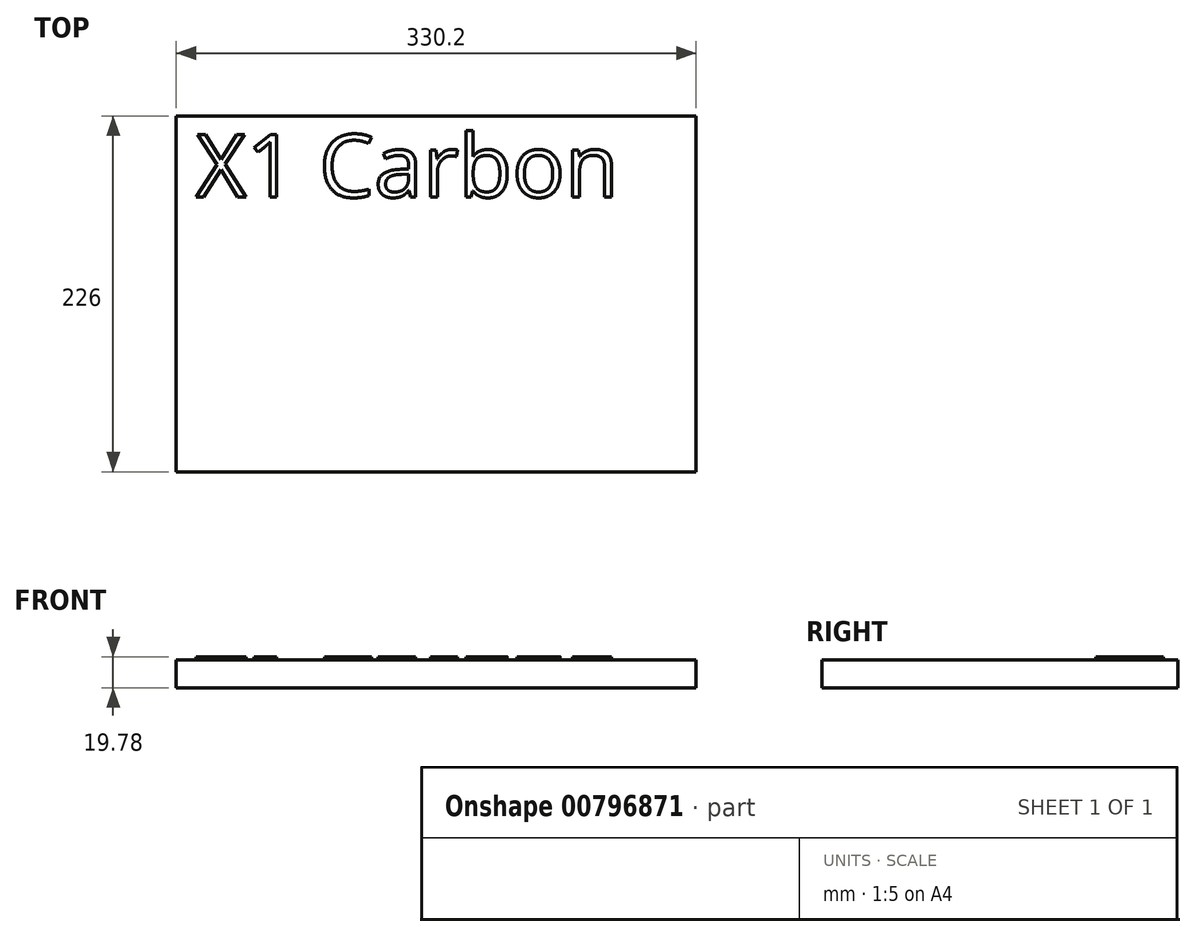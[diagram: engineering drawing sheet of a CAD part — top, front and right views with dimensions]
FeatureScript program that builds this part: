
annotation { "Feature Type Name" : "Feature", "Feature Type Description" : "" }
export const myFeature = defineFeature(function(context is Context, id is Id, definition is map)
    precondition{}
    {
        {
            var Q0;
            Q0=qCreatedBy(makeId("Top.planeOp"),FACE);
            var sketch = newSketch(context, id + "F0", { "sketchPlane" : qUnion([Q0])});
            skLineSegment(sketch, "E0.bottom", {"start": v(-174.06, 110.55) * mm, "end": v(156.14, 110.55) * mm});
            skLineSegment(sketch, "E0.top", {"start": v(-174.06, -115.45) * mm, "end": v(156.14, -115.45) * mm});
            skLineSegment(sketch, "E0.left", {"start": v(-174.06, 110.55) * mm, "end": v(-174.06, -115.45) * mm});
            skLineSegment(sketch, "E0.right", {"start": v(156.14, 110.55) * mm, "end": v(156.14, -115.45) * mm});
            skSolve(sketch);
        }
        {
            var Q0;
            Q0=makeQuery(id+"F0.imprint","IMPRINT",FACE,{"disambiguationData":[TD([[makeQuery(id+"F0.imprint","IMPRINT",EDGE,{"derivedFrom":sQuery(id+"F0.wireOp",EDGE,"E0.bottom")}),-1.0]])]});
            extrude(context, id + "F1", {"entities" : qUnion([Q0]), "depth" : 17.78 * mm, "offsetDistance" : 25 * mm});
        }
        {
            var Q0;
            Q0=makeQuery(id+"F1.opExtrude","CAP_FACE",FACE,{"disambiguationData":[OSD([sQuery(id+"F0.wireOp",EDGE,"E0.bottom"),sQuery(id+"F0.wireOp",EDGE,"E0.top"),sQuery(id+"F0.wireOp",EDGE,"E0.left"),sQuery(id+"F0.wireOp",EDGE,"E0.right")])],"isStart":false});
            var sketch = newSketch(context, id + "F2", { "sketchPlane" : qUnion([Q0])});
            skText(sketch, "E1", { "text": "X1 Carbon", "fontName": "OpenSans-Regular.ttf"});
            const initialGuessF2  = {"E1": [-0.16168, 0.05904, 1, 0, 0.04]};
            skSetInitialGuess(sketch, initialGuessF2);
            skSolve(sketch);
        }
        {
            var Q0;
            Q0=qSketchRegion(id+"F2",true);
            extrude(context, id + "F3", {"entities" : qUnion([Q0]), "operationType" : NewBodyOperationType.ADD, "depth" : 2 * mm, "offsetDistance" : 25 * mm});
        }
    });
